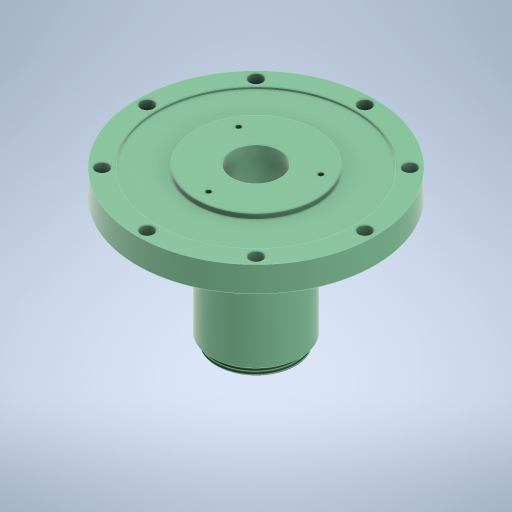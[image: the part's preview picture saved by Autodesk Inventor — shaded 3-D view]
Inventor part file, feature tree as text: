
AUTODESK INVENTOR PART (.ipt)
format: ipt  version: 2023 (Build 270158000, 158)  size: 360,448 bytes
history: native  units: mm
features: sketch x3, hole x2, pattern_circular x2, revolve x1, thread x1
ambient origin geometry x8: Origin, YZ Plane, XZ Plane, XY Plane, X Axis, Y Axis, Z Axis, Center Point
bodies: Solid1 (feature_tree)
feature tree (9):
  revolve  "Revolution1"  [1 undecoded]
  hole  "Hole2"  [1 undecoded]
  pattern_circular  "Circular Pattern2"  [2 undecoded]
  hole  "Hole3"  [1 undecoded]
  pattern_circular  "Circular Pattern3"  Count=12  [1 undecoded]
  thread  "Thread4"  [1 undecoded]
  sketch  "Sketch1"  dims[d8=360.0deg d36=110.0mm]
  sketch  "Sketch3"  dims[d38=24.0mm d39=28.0mm]
  sketch  "Sketch4"  dims[d40=45.0mm d41=1.5mm d42=12.0mm d43=120.0mm d44=61.0mm d45=55.0mm d46=6.6mm d47=12.0mm d48=12.6mm d49=2.0mm d50=90.0deg d51=17.1mm d52=0.0mm d53=80.0mm d54=360.0deg d56=1.0mm d57=100.0mm d58=0.8mm d62=24.0mm d63=2.459mm d64=6.0mm d65=4.0mm d66=2.0mm d67=90.0deg d68=8.8mm d69=20.594885mm d70=30.0mm d71=360.0deg d77=30.0mm d78=40.0mm d79=2.0mm d80=5.0mm d83=2.5mm d84=10.0mm d85=0.0mm d87=59.0mm]
note: 7 required parameter values undecoded (feature->parameter linkage not recoverable at this tier; creation-order binding heuristic only, values carry confidence <= 0.55)